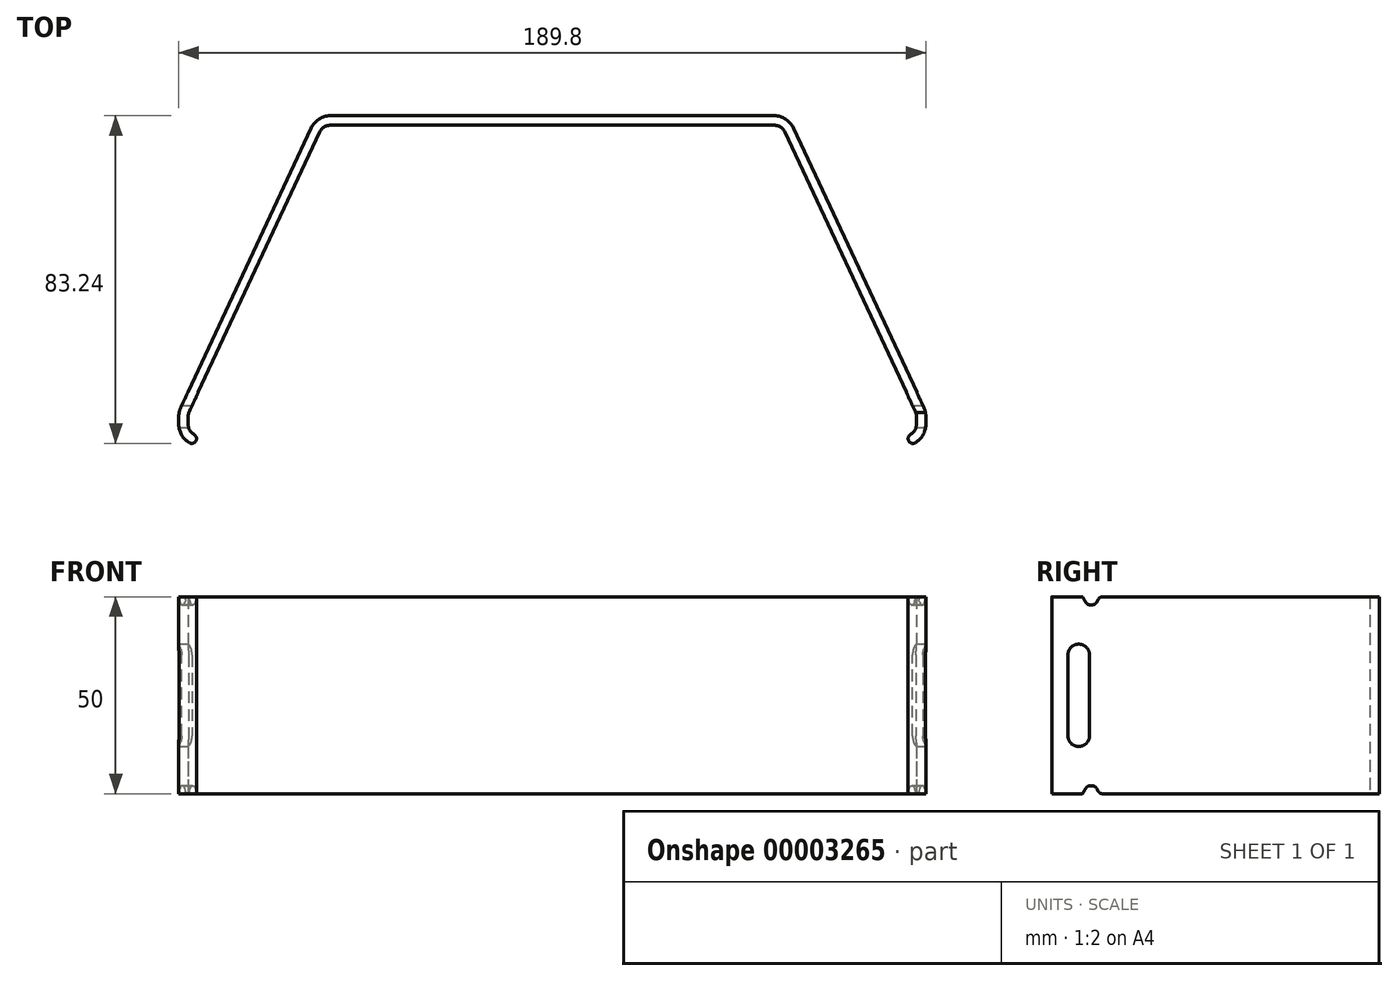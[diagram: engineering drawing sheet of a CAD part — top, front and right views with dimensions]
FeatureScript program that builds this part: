
annotation { "Feature Type Name" : "Feature", "Feature Type Description" : "" }
export const myFeature = defineFeature(function(context is Context, id is Id, definition is map)
    precondition{}
    {
        {
            var Q0;
            Q0=qCreatedBy(makeId("Top.planeOp"),FACE);
            var sketch = newSketch(context, id + "F0", { "sketchPlane" : qUnion([Q0])});
            skLineSegment(sketch, "E0", {"start": v(-56.4, 77.4) * mm, "end": v(56.4, 77.4) * mm});
            skLineSegment(sketch, "E1", {"start": v(61.29, 74.28) * mm, "end": v(94.4, 3.28) * mm});
            skLineSegment(sketch, "E2", {"start": v(94.9, 1) * mm, "end": v(94.9, -1) * mm});
            skLineSegment(sketch, "E3", {"start": v(92.5, -1) * mm, "end": v(92.5, 1) * mm});
            skLineSegment(sketch, "E4", {"start": v(92.22, 2.27) * mm, "end": v(59.11, 73.27) * mm});
            skLineSegment(sketch, "E5", {"start": v(56.4, 75) * mm, "end": v(-56.4, 75) * mm});
            skLineSegment(sketch, "E6", {"start": v(-59.11, 73.27) * mm, "end": v(-92.22, 2.27) * mm});
            skLineSegment(sketch, "E7", {"start": v(-92.5, 1) * mm, "end": v(-92.5, -1) * mm});
            skLineSegment(sketch, "E8", {"start": v(-94.9, -1) * mm, "end": v(-94.9, 1) * mm});
            skLineSegment(sketch, "E9", {"start": v(-94.4, 3.28) * mm, "end": v(-61.29, 74.28) * mm});
            skPoint(sketch, "E10.visualSharp", {"position": v(59.83, 77.4) * mm});
            skPoint(sketch, "E11.visualSharp", {"position": v(94.9, 2.2) * mm});
            skArc(sketch, "E11.filletArc", {"start": v(94.9, 1) * mm, "mid": v(94.77, 2.17) * mm, "end": v(94.4, 3.28) * mm});
            skPoint(sketch, "E12.visualSharp", {"position": v(94.9, -8) * mm});
            skArc(sketch, "E12.filletArc", {"start": v(92.2, -5.68) * mm, "mid": v(94.18, -3.7) * mm, "end": v(94.9, -1) * mm});
            skPoint(sketch, "E13.visualSharp", {"position": v(-94.9, -5.56) * mm});
            skArc(sketch, "E13.filletArc", {"start": v(-94.9, -1) * mm, "mid": v(-94.18, -3.7) * mm, "end": v(-92.2, -5.68) * mm});
            skPoint(sketch, "E14.visualSharp", {"position": v(-94.9, 2.2) * mm});
            skArc(sketch, "E14.filletArc", {"start": v(-94.4, 3.28) * mm, "mid": v(-94.77, 2.17) * mm, "end": v(-94.9, 1) * mm});
            skPoint(sketch, "E15.visualSharp", {"position": v(-59.83, 77.4) * mm});
            skArc(sketch, "E15.filletArc", {"start": v(-56.4, 77.4) * mm, "mid": v(-59.3, 76.55) * mm, "end": v(-61.29, 74.28) * mm});
            skPoint(sketch, "E16.visualSharp", {"position": v(58.3, 75) * mm});
            skArc(sketch, "E16.filletArc", {"start": v(59.11, 73.27) * mm, "mid": v(58, 74.53) * mm, "end": v(56.4, 75) * mm});
            skPoint(sketch, "E17.visualSharp", {"position": v(-58.3, 75) * mm});
            skArc(sketch, "E17.filletArc", {"start": v(-56.4, 75) * mm, "mid": v(-58, 74.53) * mm, "end": v(-59.11, 73.27) * mm});
            skPoint(sketch, "E18.visualSharp", {"position": v(-92.5, 1.67) * mm});
            skArc(sketch, "E18.filletArc", {"start": v(-92.22, 2.27) * mm, "mid": v(-92.43, 1.65) * mm, "end": v(-92.5, 1) * mm});
            skPoint(sketch, "E19.visualSharp", {"position": v(92.5, 1.67) * mm});
            skArc(sketch, "E19.filletArc", {"start": v(92.5, 1) * mm, "mid": v(92.43, 1.65) * mm, "end": v(92.22, 2.27) * mm});
            skPoint(sketch, "E20.visualSharp", {"position": v(92.5, -2.9) * mm});
            skArc(sketch, "E20.filletArc", {"start": v(91, -3.6) * mm, "mid": v(92.1, -2.5) * mm, "end": v(92.5, -1) * mm});
            skPoint(sketch, "E21.visualSharp", {"position": v(-92.5, -3) * mm});
            skArc(sketch, "E21.filletArc", {"start": v(-92.5, -1) * mm, "mid": v(-92.1, -2.5) * mm, "end": v(-91, -3.6) * mm});
            skLineSegment(sketch, "E22", {"start": v(92.5, 0) * mm, "end": v(-92.5, 0) * mm, "construction": true});
            skArc(sketch, "E23", {"start": v(-92.2, -5.68) * mm, "mid": v(-90.56, -5.24) * mm, "end": v(-91, -3.6) * mm});
            skArc(sketch, "E24", {"start": v(91, -3.6) * mm, "mid": v(90.56, -5.24) * mm, "end": v(92.2, -5.68) * mm});
            skArc(sketch, "E25", {"start": v(61.29, 74.28) * mm, "mid": v(59.3, 76.55) * mm, "end": v(56.4, 77.4) * mm});
            skLineSegment(sketch, "E26", {"start": v(-89.5, -1) * mm, "end": v(-91.6, -4.64) * mm, "construction": true});
            skLineSegment(sketch, "E27", {"start": v(89.5, -1) * mm, "end": v(91.6, -4.64) * mm, "construction": true});
            skSolve(sketch);
        }
        {
            var Q0;
            Q0=qSketchRegion(id+"F0",true);
            extrude(context, id + "F1", {"entities" : qUnion([Q0]), "endBound" : BoundingType.SYMMETRIC, "depth" : 50 * mm});
        }
        {
            var Q0;
            Q0=qCreatedBy(makeId("Right.planeOp"),FACE);
            var sketch = newSketch(context, id + "F2", { "sketchPlane" : qUnion([Q0])});
            skLineSegment(sketch, "E28", {"start": v(3.75, 10.25) * mm, "end": v(3.75, -10.25) * mm});
            skLineSegment(sketch, "E29", {"start": v(-1.75, 10.25) * mm, "end": v(-1.75, -10.25) * mm});
            skArc(sketch, "E30", {"start": v(3.75, 10.25) * mm, "mid": v(1, 13) * mm, "end": v(-1.75, 10.25) * mm});
            skArc(sketch, "E31", {"start": v(3.75, -10.25) * mm, "mid": v(1, -13) * mm, "end": v(-1.75, -10.25) * mm});
            skLineSegment(sketch, "E32", {"start": v(1, 10.25) * mm, "end": v(1, -10.25) * mm, "construction": true});
            skLineSegment(sketch, "E33", {"start": v(1, 0) * mm, "end": v(0, 0) * mm, "construction": true});
            skLineSegment(sketch, "E34", {"start": v(1, 13) * mm, "end": v(1, 25) * mm, "construction": true});
            skSolve(sketch);
        }
        {
            var Q0;
            Q0=qSketchRegion(id+"F2",true);
            extrude(context, id + "F3", {"entities" : qUnion([Q0]), "operationType" : NewBodyOperationType.REMOVE, "endBound" : BoundingType.THROUGH_ALL, "oppositeDirection" : true, "depth" : 25 * mm, "hasSecondDirection" : true, "secondDirectionBound" : SecondDirectionBoundingType.THROUGH_ALL, "secondDirectionOppositeDirection" : false, "secondDirectionDepth" : 25 * mm});
        }
        {
            var Q0;
            Q0=qCreatedBy(makeId("Right.planeOp"),FACE);
            var sketch = newSketch(context, id + "F4", { "sketchPlane" : qUnion([Q0])});
            skLineSegment(sketch, "E35", {"start": v(2, 25) * mm, "end": v(2, 25) * mm});
            skLineSegment(sketch, "E36", {"start": v(2, 25) * mm, "end": v(3.15, 23) * mm});
            skLineSegment(sketch, "E37", {"start": v(3.15, 23) * mm, "end": v(5.15, 23) * mm});
            skLineSegment(sketch, "E38", {"start": v(5.15, 23) * mm, "end": v(6.3, 25) * mm});
            skLineSegment(sketch, "E39", {"start": v(6.3, 25) * mm, "end": v(2, 25) * mm});
            skLineSegment(sketch, "E40", {"start": v(0, 0) * mm, "end": v(-15.35, 0) * mm, "construction": true});
            skLineSegment(sketch, "E41.MirrorCS", {"start": v(6.3, -25) * mm, "end": v(2, -25) * mm});
            skLineSegment(sketch, "E42.MirrorCS", {"start": v(3.15, -23) * mm, "end": v(5.15, -23) * mm});
            skLineSegment(sketch, "E43.MirrorCS", {"start": v(5.15, -23) * mm, "end": v(6.3, -25) * mm});
            skLineSegment(sketch, "E44.MirrorCS", {"start": v(2, -25) * mm, "end": v(2, -25) * mm});
            skLineSegment(sketch, "E45.MirrorCS", {"start": v(2, -25) * mm, "end": v(3.15, -23) * mm});
            skLineSegment(sketch, "E46", {"start": v(0, 0) * mm, "end": v(2, 0) * mm, "construction": true});
            skLineSegment(sketch, "E47", {"start": v(2, 25) * mm, "end": v(2, -25) * mm, "construction": true});
            skSolve(sketch);
        }
        {
            var Q0;
            Q0=qSketchRegion(id+"F4",true);
            extrude(context, id + "F5", {"entities" : qUnion([Q0]), "operationType" : NewBodyOperationType.REMOVE, "endBound" : BoundingType.THROUGH_ALL, "oppositeDirection" : true, "depth" : 25 * mm, "hasSecondDirection" : true, "secondDirectionBound" : SecondDirectionBoundingType.THROUGH_ALL, "secondDirectionOppositeDirection" : false, "secondDirectionDepth" : 25 * mm});
        }
        {
            var Q0;
            Q0=makeQuery(id+"F5.boolean.opBoolean","COPY",EDGE,{"disambiguationData":[OD(0.0)],"derivedFrom":makeQuery(id+"F5.opExtrude","SWEPT_EDGE",EDGE,{"disambiguationData":[OSD([sQuery(id+"F4.wireOp",EDGE,"E36"),sQuery(id+"F4.wireOp",EDGE,"E39")])]})});
            var Q1;
            Q1=makeQuery(id+"F5.boolean.opBoolean","COPY",EDGE,{"disambiguationData":[OD(1.0)],"derivedFrom":makeQuery(id+"F5.opExtrude","SWEPT_EDGE",EDGE,{"disambiguationData":[OSD([sQuery(id+"F4.wireOp",EDGE,"E36"),sQuery(id+"F4.wireOp",EDGE,"E39")])]})});
            var Q2;
            Q2=makeQuery(id+"F5.boolean.opBoolean","COPY",EDGE,{"disambiguationData":[OD(0.0)],"derivedFrom":makeQuery(id+"F5.opExtrude","SWEPT_EDGE",EDGE,{"disambiguationData":[OSD([sQuery(id+"F4.wireOp",EDGE,"E38"),sQuery(id+"F4.wireOp",EDGE,"E39")])]})});
            var Q3;
            Q3=makeQuery(id+"F5.boolean.opBoolean","COPY",EDGE,{"disambiguationData":[OD(1.0)],"derivedFrom":makeQuery(id+"F5.opExtrude","SWEPT_EDGE",EDGE,{"disambiguationData":[OSD([sQuery(id+"F4.wireOp",EDGE,"E38"),sQuery(id+"F4.wireOp",EDGE,"E39")])]})});
            var Q4;
            Q4=makeQuery(id+"F5.boolean.opBoolean","COPY",EDGE,{"disambiguationData":[OD(0.0)],"derivedFrom":makeQuery(id+"F5.opExtrude","SWEPT_EDGE",EDGE,{"disambiguationData":[OSD([sQuery(id+"F4.wireOp",EDGE,"E41.MirrorCS"),sQuery(id+"F4.wireOp",EDGE,"E43.MirrorCS")])]})});
            var Q5;
            Q5=makeQuery(id+"F5.boolean.opBoolean","COPY",EDGE,{"disambiguationData":[OD(0.0)],"derivedFrom":makeQuery(id+"F5.opExtrude","SWEPT_EDGE",EDGE,{"disambiguationData":[OSD([sQuery(id+"F4.wireOp",EDGE,"E41.MirrorCS"),sQuery(id+"F4.wireOp",EDGE,"E45.MirrorCS")])]})});
            var Q6;
            Q6=makeQuery(id+"F5.boolean.opBoolean","COPY",EDGE,{"disambiguationData":[OD(1.0)],"derivedFrom":makeQuery(id+"F5.opExtrude","SWEPT_EDGE",EDGE,{"disambiguationData":[OSD([sQuery(id+"F4.wireOp",EDGE,"E41.MirrorCS"),sQuery(id+"F4.wireOp",EDGE,"E43.MirrorCS")])]})});
            var Q7;
            Q7=makeQuery(id+"F5.boolean.opBoolean","COPY",EDGE,{"disambiguationData":[OD(1.0)],"derivedFrom":makeQuery(id+"F5.opExtrude","SWEPT_EDGE",EDGE,{"disambiguationData":[OSD([sQuery(id+"F4.wireOp",EDGE,"E41.MirrorCS"),sQuery(id+"F4.wireOp",EDGE,"E45.MirrorCS")])]})});
            var Q8;
            Q8=makeQuery(id+"F5.boolean.opBoolean","COPY",EDGE,{"disambiguationData":[OD(1.0)],"derivedFrom":makeQuery(id+"F5.opExtrude","SWEPT_EDGE",EDGE,{"disambiguationData":[OSD([sQuery(id+"F4.wireOp",EDGE,"E37"),sQuery(id+"F4.wireOp",EDGE,"E38")])]})});
            var Q9;
            Q9=makeQuery(id+"F5.boolean.opBoolean","COPY",EDGE,{"disambiguationData":[OD(1.0)],"derivedFrom":makeQuery(id+"F5.opExtrude","SWEPT_EDGE",EDGE,{"disambiguationData":[OSD([sQuery(id+"F4.wireOp",EDGE,"E36"),sQuery(id+"F4.wireOp",EDGE,"E37")])]})});
            var Q10;
            Q10=makeQuery(id+"F5.boolean.opBoolean","COPY",EDGE,{"disambiguationData":[OD(1.0)],"derivedFrom":makeQuery(id+"F5.opExtrude","SWEPT_EDGE",EDGE,{"disambiguationData":[OSD([sQuery(id+"F4.wireOp",EDGE,"E42.MirrorCS"),sQuery(id+"F4.wireOp",EDGE,"E43.MirrorCS")])]})});
            var Q11;
            Q11=makeQuery(id+"F5.boolean.opBoolean","COPY",EDGE,{"disambiguationData":[OD(1.0)],"derivedFrom":makeQuery(id+"F5.opExtrude","SWEPT_EDGE",EDGE,{"disambiguationData":[OSD([sQuery(id+"F4.wireOp",EDGE,"E42.MirrorCS"),sQuery(id+"F4.wireOp",EDGE,"E45.MirrorCS")])]})});
            var Q12;
            Q12=makeQuery(id+"F5.boolean.opBoolean","COPY",EDGE,{"disambiguationData":[OD(0.0)],"derivedFrom":makeQuery(id+"F5.opExtrude","SWEPT_EDGE",EDGE,{"disambiguationData":[OSD([sQuery(id+"F4.wireOp",EDGE,"E42.MirrorCS"),sQuery(id+"F4.wireOp",EDGE,"E43.MirrorCS")])]})});
            var Q13;
            Q13=makeQuery(id+"F5.boolean.opBoolean","COPY",EDGE,{"disambiguationData":[OD(0.0)],"derivedFrom":makeQuery(id+"F5.opExtrude","SWEPT_EDGE",EDGE,{"disambiguationData":[OSD([sQuery(id+"F4.wireOp",EDGE,"E42.MirrorCS"),sQuery(id+"F4.wireOp",EDGE,"E45.MirrorCS")])]})});
            var Q14;
            Q14=makeQuery(id+"F5.boolean.opBoolean","COPY",EDGE,{"disambiguationData":[OD(0.0)],"derivedFrom":makeQuery(id+"F5.opExtrude","SWEPT_EDGE",EDGE,{"disambiguationData":[OSD([sQuery(id+"F4.wireOp",EDGE,"E37"),sQuery(id+"F4.wireOp",EDGE,"E38")])]})});
            var Q15;
            Q15=makeQuery(id+"F5.boolean.opBoolean","COPY",EDGE,{"disambiguationData":[OD(0.0)],"derivedFrom":makeQuery(id+"F5.opExtrude","SWEPT_EDGE",EDGE,{"disambiguationData":[OSD([sQuery(id+"F4.wireOp",EDGE,"E36"),sQuery(id+"F4.wireOp",EDGE,"E37")])]})});
            fillet(context, id + "F6", {"entities" : qUnion([Q0, Q1, Q2, Q3, Q4, Q5, Q6, Q7, Q8, Q9, Q10, Q11, Q12, Q13, Q14, Q15]), "radius" : 1.5 * mm, "tangentPropagation" : true, "rho" : .6, "crossSection" : FilletCrossSection.CONIC, "allowEdgeOverflow" : false});
        }
    });
